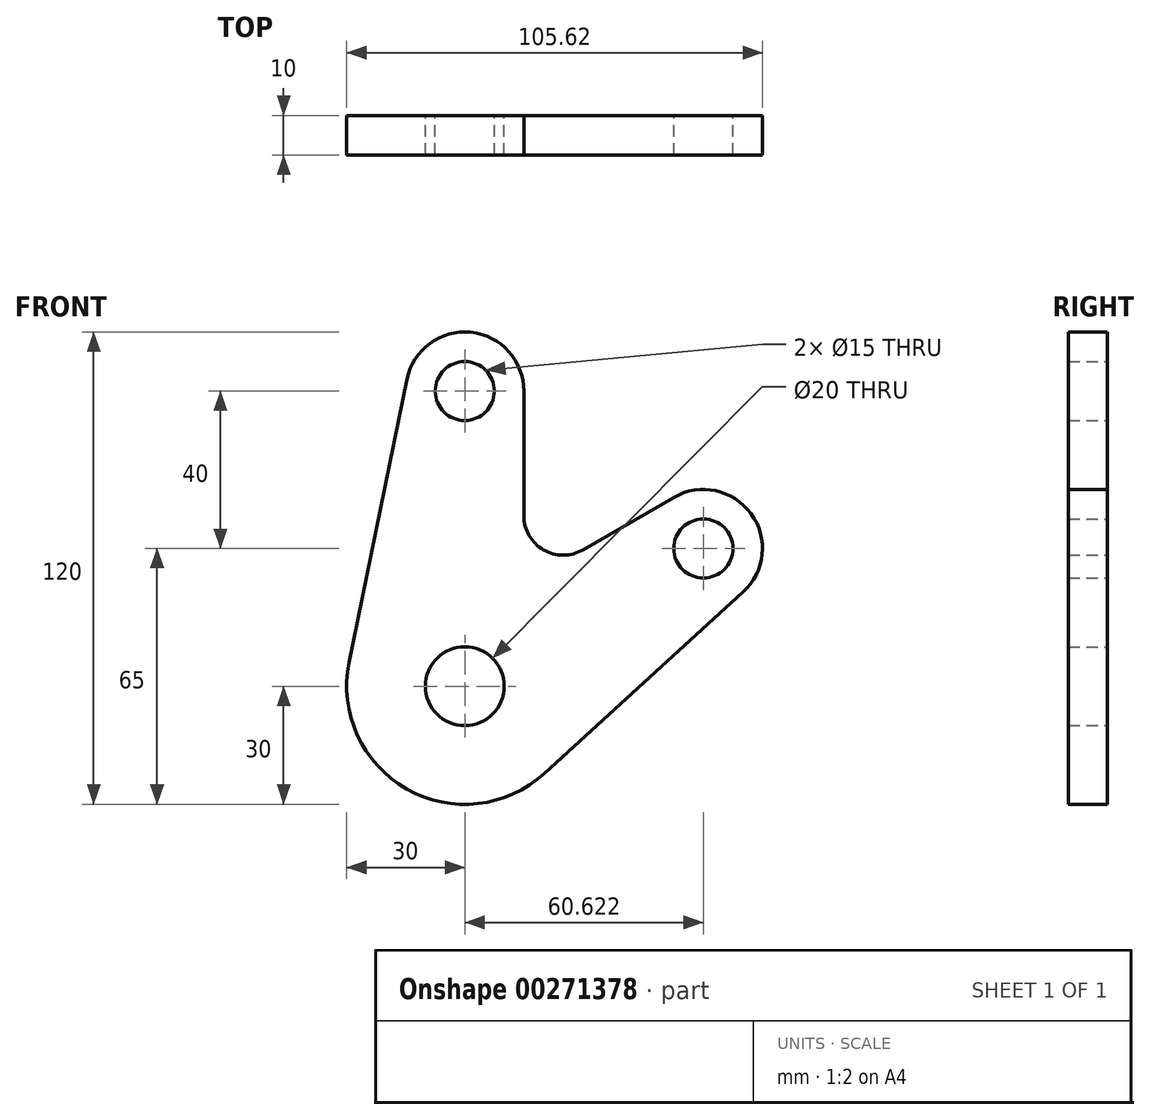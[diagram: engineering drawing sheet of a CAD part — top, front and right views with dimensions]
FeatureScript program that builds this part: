
annotation { "Feature Type Name" : "Feature", "Feature Type Description" : "" }
export const myFeature = defineFeature(function(context is Context, id is Id, definition is map)
    precondition{}
    {
        {
            var Q0;
            Q0=qCreatedBy(makeId("Front.planeOp"),FACE);
            var sketch = newSketch(context, id + "F0", { "sketchPlane" : qUnion([Q0])});
            skCircle(sketch, "E0", {"center": v(0, 0) * mm, "radius": 10 * mm});
            skCircle(sketch, "E1", {"center": v(60.62, 35) * mm, "radius": 7.5 * mm});
            skCircle(sketch, "E2", {"center": v(0, 75) * mm, "radius": 7.5 * mm});
            skLineSegment(sketch, "E3", {"start": v(-14.7, 78) * mm, "end": v(-29.4, 6) * mm});
            skLineSegment(sketch, "E4", {"start": v(70.73, 23.92) * mm, "end": v(20.22, -22.16) * mm});
            skLineSegment(sketch, "E5", {"start": v(53.12, 48) * mm, "end": v(30, 34.64) * mm});
            skLineSegment(sketch, "E6", {"start": v(15, 75) * mm, "end": v(15, 43.3) * mm});
            skArc(sketch, "E7.filletArc", {"start": v(15, 75) * mm, "mid": v(1.5, 89.92) * mm, "end": v(-14.7, 78) * mm});
            skArc(sketch, "E8.filletArc", {"start": v(15, 43.3) * mm, "mid": v(20, 34.64) * mm, "end": v(30, 34.64) * mm});
            skArc(sketch, "E9.filletArc", {"start": v(-29.4, 6) * mm, "mid": v(-14.8, -26.09) * mm, "end": v(20.22, -22.16) * mm});
            skArc(sketch, "E10", {"start": v(53.12, 48) * mm, "mid": v(72.73, 43.86) * mm, "end": v(70.73, 23.92) * mm});
            skLineSegment(sketch, "E11", {"start": v(0, 75) * mm, "end": v(0, 0) * mm, "construction": true});
            skLineSegment(sketch, "E12", {"start": v(60.62, 35) * mm, "end": v(0, 0) * mm, "construction": true});
            skSolve(sketch);
        }
        {
            var Q0;
            Q0=makeQuery(id+"F0.imprint","IMPRINT",FACE,{"disambiguationData":[TD([[makeQuery(id+"F0.imprint","IMPRINT",EDGE,{"derivedFrom":sQuery(id+"F0.wireOp",EDGE,"E0")}),-1.0]])]});
            extrude(context, id + "F1", {"entities" : qUnion([Q0]), "depth" : 10 * mm});
        }
    });
